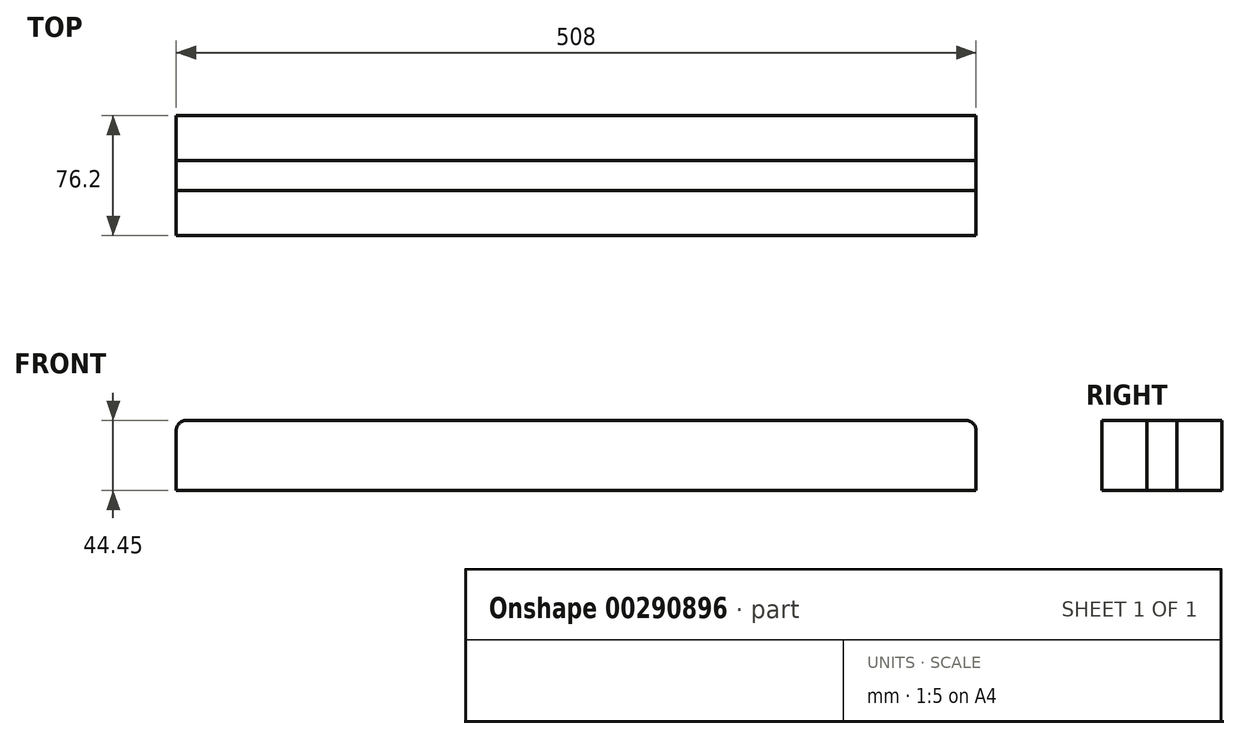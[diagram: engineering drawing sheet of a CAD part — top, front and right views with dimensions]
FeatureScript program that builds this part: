
annotation { "Feature Type Name" : "Feature", "Feature Type Description" : "" }
export const myFeature = defineFeature(function(context is Context, id is Id, definition is map)
    precondition{}
    {
        {
            var Q0;
            Q0=qCreatedBy(makeId("Top.planeOp"),FACE);
            var sketch = newSketch(context, id + "F0", { "sketchPlane" : qUnion([Q0])});
            skLineSegment(sketch, "E0.bottom", {"start": v(-254, 14.29) * mm, "end": v(254, 14.29) * mm});
            skLineSegment(sketch, "E0.top", {"start": v(-254, -14.29) * mm, "end": v(254, -14.29) * mm});
            skLineSegment(sketch, "E0.left", {"start": v(-254, 14.29) * mm, "end": v(-254, -14.29) * mm});
            skLineSegment(sketch, "E0.right", {"start": v(254, 14.29) * mm, "end": v(254, -14.29) * mm});
            skSolve(sketch);
        }
        {
            var Q0;
            Q0=makeQuery(id+"F0.imprint","IMPRINT",FACE,{"disambiguationData":[TD([[makeQuery(id+"F0.imprint","IMPRINT",EDGE,{"derivedFrom":sQuery(id+"F0.wireOp",EDGE,"E0.bottom")}),-1.0]])]});
            extrude(context, id + "F1", {"entities" : qUnion([Q0]), "depth" : 44.45 * mm});
        }
        {
            var Q0;
            Q0=qCreatedBy(makeId("Top.planeOp"),FACE);
            var sketch = newSketch(context, id + "F2", { "sketchPlane" : qUnion([Q0])});
            skLineSegment(sketch, "E1.bottom", {"start": v(-254, 33.34) * mm, "end": v(254, 33.34) * mm});
            skLineSegment(sketch, "E1.top", {"start": v(-254, 14.29) * mm, "end": v(254, 14.29) * mm});
            skLineSegment(sketch, "E1.left", {"start": v(-254, 33.34) * mm, "end": v(-254, 14.29) * mm});
            skLineSegment(sketch, "E1.right", {"start": v(254, 33.34) * mm, "end": v(254, 14.29) * mm});
            skSolve(sketch);
        }
        {
            var Q0;
            Q0=makeQuery(id+"F2.imprint","IMPRINT",FACE,{"disambiguationData":[TD([[makeQuery(id+"F2.imprint","IMPRINT",EDGE,{"derivedFrom":sQuery(id+"F2.wireOp",EDGE,"E1.bottom")}),-1.0]])]});
            var Q1;
            Q1=makeQuery(id+"F1.opExtrude","CAP_FACE",FACE,{"disambiguationData":[OSD([sQuery(id+"F0.wireOp",EDGE,"E0.bottom"),sQuery(id+"F0.wireOp",EDGE,"E0.top"),sQuery(id+"F0.wireOp",EDGE,"E0.left"),sQuery(id+"F0.wireOp",EDGE,"E0.right")])],"isStart":false});
            extrude(context, id + "F3", {"entities" : qUnion([Q0]), "endBound" : BoundingType.UP_TO_SURFACE, "endBoundEntityFace" : qUnion([Q1]), "depth" : 25.4 * mm});
        }
        {
            var Q0;
            Q0=qCreatedBy(makeId("Top.planeOp"),FACE);
            var sketch = newSketch(context, id + "F4", { "sketchPlane" : qUnion([Q0])});
            skLineSegment(sketch, "E2.bottom", {"start": v(-254, 61.91) * mm, "end": v(254, 61.91) * mm});
            skLineSegment(sketch, "E2.top", {"start": v(-254, 33.34) * mm, "end": v(254, 33.34) * mm});
            skLineSegment(sketch, "E2.left", {"start": v(-254, 61.91) * mm, "end": v(-254, 33.34) * mm});
            skLineSegment(sketch, "E2.right", {"start": v(254, 61.91) * mm, "end": v(254, 33.34) * mm});
            skSolve(sketch);
        }
        {
            var Q0;
            Q0=makeQuery(id+"F4.imprint","IMPRINT",FACE,{"disambiguationData":[TD([[makeQuery(id+"F4.imprint","IMPRINT",EDGE,{"derivedFrom":sQuery(id+"F4.wireOp",EDGE,"E2.bottom")}),-1.0]])]});
            var Q1;
            Q1=makeQuery(id+"F1.opExtrude","CAP_FACE",FACE,{"disambiguationData":[OSD([sQuery(id+"F0.wireOp",EDGE,"E0.bottom"),sQuery(id+"F0.wireOp",EDGE,"E0.top"),sQuery(id+"F0.wireOp",EDGE,"E0.left"),sQuery(id+"F0.wireOp",EDGE,"E0.right")])],"isStart":false});
            extrude(context, id + "F5", {"entities" : qUnion([Q0]), "endBound" : BoundingType.UP_TO_SURFACE, "endBoundEntityFace" : qUnion([Q1]), "depth" : 25.4 * mm});
        }
        {
            var Q0;
            Q0=qCreatedBy(makeId("Front.planeOp"),FACE);
            var sketch = newSketch(context, id + "F6", { "sketchPlane" : qUnion([Q0])});
            skArc(sketch, "E3", {"start": v(254, 38.1) * mm, "mid": v(252.14, 42.6) * mm, "end": v(247.65, 44.45) * mm});
            skLineSegment(sketch, "E4", {"start": v(247.65, 44.45) * mm, "end": v(254, 44.45) * mm});
            skLineSegment(sketch, "E5", {"start": v(254, 44.45) * mm, "end": v(254, 38.1) * mm});
            skArc(sketch, "E6.MirrorCS", {"start": v(-254, 38.1) * mm, "mid": v(-252.14, 42.6) * mm, "end": v(-247.65, 44.45) * mm});
            skLineSegment(sketch, "E7.MirrorCS", {"start": v(-247.65, 44.45) * mm, "end": v(-254, 44.45) * mm});
            skLineSegment(sketch, "E8.MirrorCS", {"start": v(-254, 44.45) * mm, "end": v(-254, 38.1) * mm});
            skSolve(sketch);
        }
        {
            var Q0;
            Q0 = qSketchRegion(id + "F6", true);
            extrude(context, id + "F7", {"entities" : qUnion([Q0]), "operationType" : NewBodyOperationType.REMOVE, "endBound" : BoundingType.THROUGH_ALL, "oppositeDirection" : true, "depth" : 25.4 * mm, "hasSecondDirection" : true, "secondDirectionBound" : SecondDirectionBoundingType.THROUGH_ALL, "secondDirectionOppositeDirection" : false, "secondDirectionDepth" : 25.4 * mm});
        }
        {
            var Q0;
            Q0 = qSketchRegion(id + "F6", true);
            extrude(context, id + "F8", {"entities" : qUnion([Q0]), "operationType" : NewBodyOperationType.REMOVE, "endBound" : BoundingType.THROUGH_ALL, "oppositeDirection" : true, "depth" : 32.77 * mm});
        }
        {
            var Q0;
            Q0 = qSketchRegion(id + "F6", true);
            extrude(context, id + "F9", {"entities" : qUnion([Q0]), "operationType" : NewBodyOperationType.REMOVE, "endBound" : BoundingType.THROUGH_ALL, "oppositeDirection" : true, "depth" : 75.95 * mm});
        }
    });
